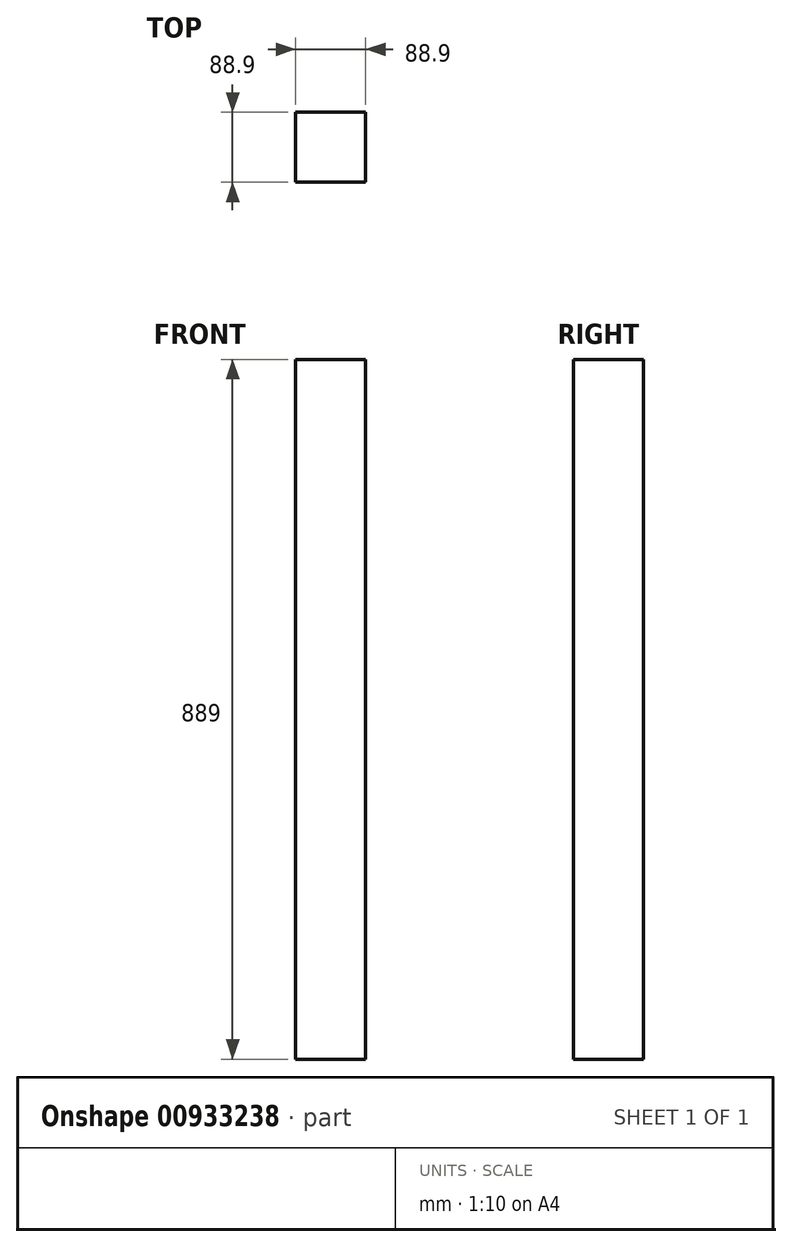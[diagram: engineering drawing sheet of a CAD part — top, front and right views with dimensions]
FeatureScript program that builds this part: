
annotation { "Feature Type Name" : "Feature", "Feature Type Description" : "" }
export const myFeature = defineFeature(function(context is Context, id is Id, definition is map)
    precondition{}
    {
        {
            var Q0;
            Q0=qCreatedBy(makeId("Front.planeOp"),FACE);
            var sketch = newSketch(context, id + "F0", { "sketchPlane" : qUnion([Q0])});
            skLineSegment(sketch, "E0.bottom", {"start": v(-44.45, -444.5) * mm, "end": v(44.45, -444.5) * mm});
            skLineSegment(sketch, "E0.top", {"start": v(-44.45, 444.5) * mm, "end": v(44.45, 444.5) * mm});
            skLineSegment(sketch, "E0.left", {"start": v(-44.45, -444.5) * mm, "end": v(-44.45, 444.5) * mm});
            skLineSegment(sketch, "E0.right", {"start": v(44.45, -444.5) * mm, "end": v(44.45, 444.5) * mm});
            skPoint(sketch, "E0.middle", {"position": v(0, 0) * mm});
            skSolve(sketch);
        }
        {
            var Q0;
            Q0=qSketchRegion(id+"F0",true);
            extrude(context, id + "F1", {"entities" : qUnion([Q0]), "depth" : 88.9 * mm, "offsetDistance" : 25.4 * mm});
        }
    });
